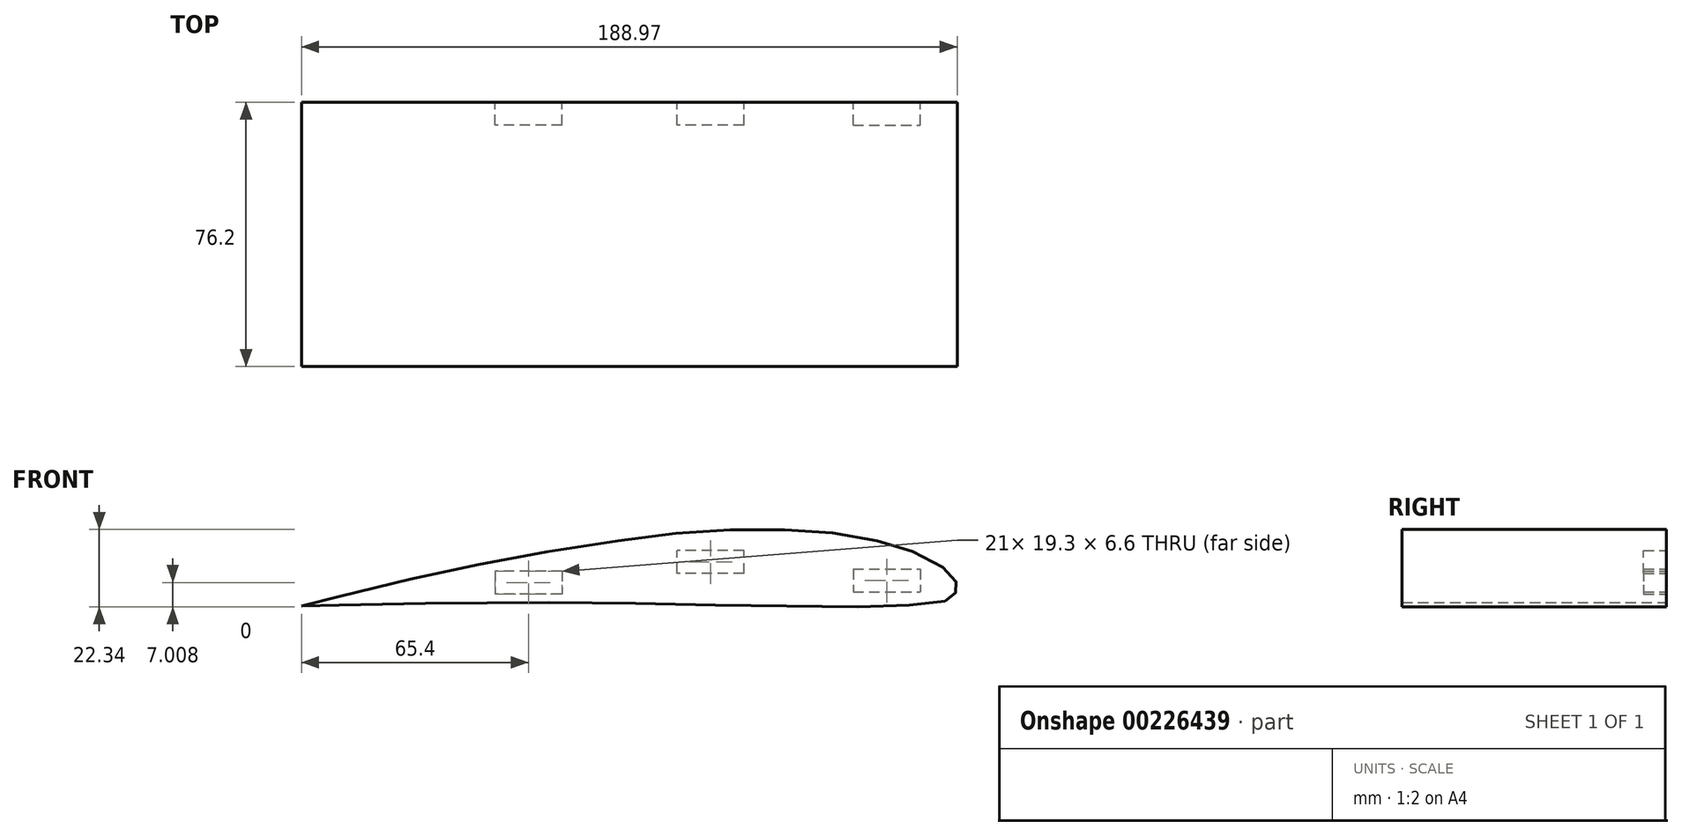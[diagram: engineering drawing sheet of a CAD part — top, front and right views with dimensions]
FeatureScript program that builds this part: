
annotation { "Feature Type Name" : "Feature", "Feature Type Description" : "" }
export const myFeature = defineFeature(function(context is Context, id is Id, definition is map)
    precondition{}
    {
        {
            var Q0;
            Q0=qCreatedBy(makeId("Front.planeOp"),FACE);
            var sketch = newSketch(context, id + "F0", { "sketchPlane" : qUnion([Q0])});
            skPoint(sketch, "E0.0", {"position": v(-50.76, -2.1) * mm});
            skPoint(sketch, "E0.1", {"position": v(1.67, 3.8) * mm});
            skPoint(sketch, "E0.2", {"position": v(52.47, -1.53) * mm});
            skLineSegment(sketch, "E1.bottom", {"start": v(-41.1, 1.2) * mm, "end": v(-60.41, 1.2) * mm});
            skLineSegment(sketch, "E1.top", {"start": v(-41.1, -5.4) * mm, "end": v(-60.41, -5.4) * mm});
            skLineSegment(sketch, "E1.left", {"start": v(-41.1, 1.2) * mm, "end": v(-41.1, -5.4) * mm});
            skLineSegment(sketch, "E1.right", {"start": v(-60.41, 1.2) * mm, "end": v(-60.41, -5.4) * mm});
            skLineSegment(sketch, "E2.bottom", {"start": v(11.32, 0.5) * mm, "end": v(-7.98, 0.5) * mm});
            skLineSegment(sketch, "E2.top", {"start": v(11.32, 7.11) * mm, "end": v(-7.98, 7.11) * mm});
            skLineSegment(sketch, "E2.left", {"start": v(11.32, 0.5) * mm, "end": v(11.32, 7.11) * mm});
            skLineSegment(sketch, "E2.right", {"start": v(-7.98, 0.5) * mm, "end": v(-7.98, 7.11) * mm});
            skLineSegment(sketch, "E3.bottom", {"start": v(42.82, 1.78) * mm, "end": v(62.12, 1.78) * mm});
            skLineSegment(sketch, "E3.top", {"start": v(42.82, -4.83) * mm, "end": v(62.12, -4.83) * mm});
            skLineSegment(sketch, "E3.left", {"start": v(42.82, 1.78) * mm, "end": v(42.82, -4.83) * mm});
            skLineSegment(sketch, "E3.right", {"start": v(62.12, 1.78) * mm, "end": v(62.12, -4.83) * mm});
            skFitSpline(sketch, "E4.0", {"points": [v(-116.13, -8.86) * mm, v(-116.1, -8.92) * mm, v(-113.34, -8.82) * mm, v(-102.32, -8.55) * mm, v(-58.98, -7.89) * mm, v(-19.88, -8.13) * mm, v(-18.68, -8.15) * mm, v(44.47, -9.1) * mm, v(56.23, -8.67) * mm, v(63.71, -8.44) * mm, v(68.49, -7.65) * mm, v(69.72, -7.28) * mm, v(70.48, -6.93) * mm, v(71.17, -6.45) * mm, v(71.78, -5.86) * mm, v(72.2, -5.27) * mm, v(72.5, -4.73) * mm, v(72.68, -4.2) * mm, v(72.76, -3.87) * mm, v(72.8, -3.4) * mm, v(72.77, -2.9) * mm, v(72.64, -2.33) * mm, v(72.38, -1.68) * mm, v(71.8, -0.7) * mm, v(70.96, 0.3) * mm, v(69.44, 1.7) * mm, v(66.99, 3.34) * mm, v(62.33, 5.84) * mm, v(57.69, 7.82) * mm, v(52.6, 9.28) * mm, v(45, 10.94) * mm, v(36.71, 12.19) * mm, v(27.48, 12.97) * mm, v(16.95, 13.22) * mm, v(4.36, 13) * mm, v(-7.87, 12.1) * mm, v(-20.45, 10.6) * mm, v(-40.4, 7.54) * mm, v(-60.73, 4.03) * mm, v(-78.8, 0.18) * mm, v(-100.8, -4.93) * mm, v(-113.29, -8.2) * mm, v(-116.16, -8.8) * mm, v(-116.13, -8.86) * mm]});
            skSolve(sketch);
        }
        {
            var Q0;
            Q0=makeQuery(id+"F0.imprint","IMPRINT",FACE,{"disambiguationData":[TD([[makeQuery(id+"F0.imprint","IMPRINT",EDGE,{"derivedFrom":sQuery(id+"F0.wireOp",EDGE,"E1.bottom")}),-1.0]])]});
            var Q1;
            Q1=makeQuery(id+"F0.imprint","IMPRINT",FACE,{"disambiguationData":[TD([[makeQuery(id+"F0.imprint","IMPRINT",EDGE,{"derivedFrom":sQuery(id+"F0.wireOp",EDGE,"E1.bottom")}),1.0]])]});
            var Q2;
            Q2=makeQuery(id+"F0.imprint","IMPRINT",FACE,{"disambiguationData":[TD([[makeQuery(id+"F0.imprint","IMPRINT",EDGE,{"derivedFrom":sQuery(id+"F0.wireOp",EDGE,"E2.bottom")}),-1.0]])]});
            var Q3;
            Q3=makeQuery(id+"F0.imprint","IMPRINT",FACE,{"disambiguationData":[TD([[makeQuery(id+"F0.imprint","IMPRINT",EDGE,{"derivedFrom":sQuery(id+"F0.wireOp",EDGE,"E3.bottom")}),-1.0]])]});
            extrude(context, id + "F1", {"entities" : qUnion([Q0, Q1, Q2, Q3]), "depth" : 76.2 * mm});
        }
        {
            var Q0;
            Q0=makeQuery(id+"F0.imprint","IMPRINT",FACE,{"disambiguationData":[TD([[makeQuery(id+"F0.imprint","IMPRINT",EDGE,{"derivedFrom":sQuery(id+"F0.wireOp",EDGE,"E2.bottom")}),-1.0]])]});
            var Q1;
            Q1=makeQuery(id+"F0.imprint","IMPRINT",FACE,{"disambiguationData":[TD([[makeQuery(id+"F0.imprint","IMPRINT",EDGE,{"derivedFrom":sQuery(id+"F0.wireOp",EDGE,"E3.bottom")}),-1.0]])]});
            var Q2;
            Q2=makeQuery(id+"F0.imprint","IMPRINT",FACE,{"disambiguationData":[TD([[makeQuery(id+"F0.imprint","IMPRINT",EDGE,{"derivedFrom":sQuery(id+"F0.wireOp",EDGE,"E1.bottom")}),1.0]])]});
            extrude(context, id + "F2", {"entities" : qUnion([Q0, Q1, Q2]), "operationType" : NewBodyOperationType.REMOVE, "depth" : 6.6 * mm});
        }
    });
